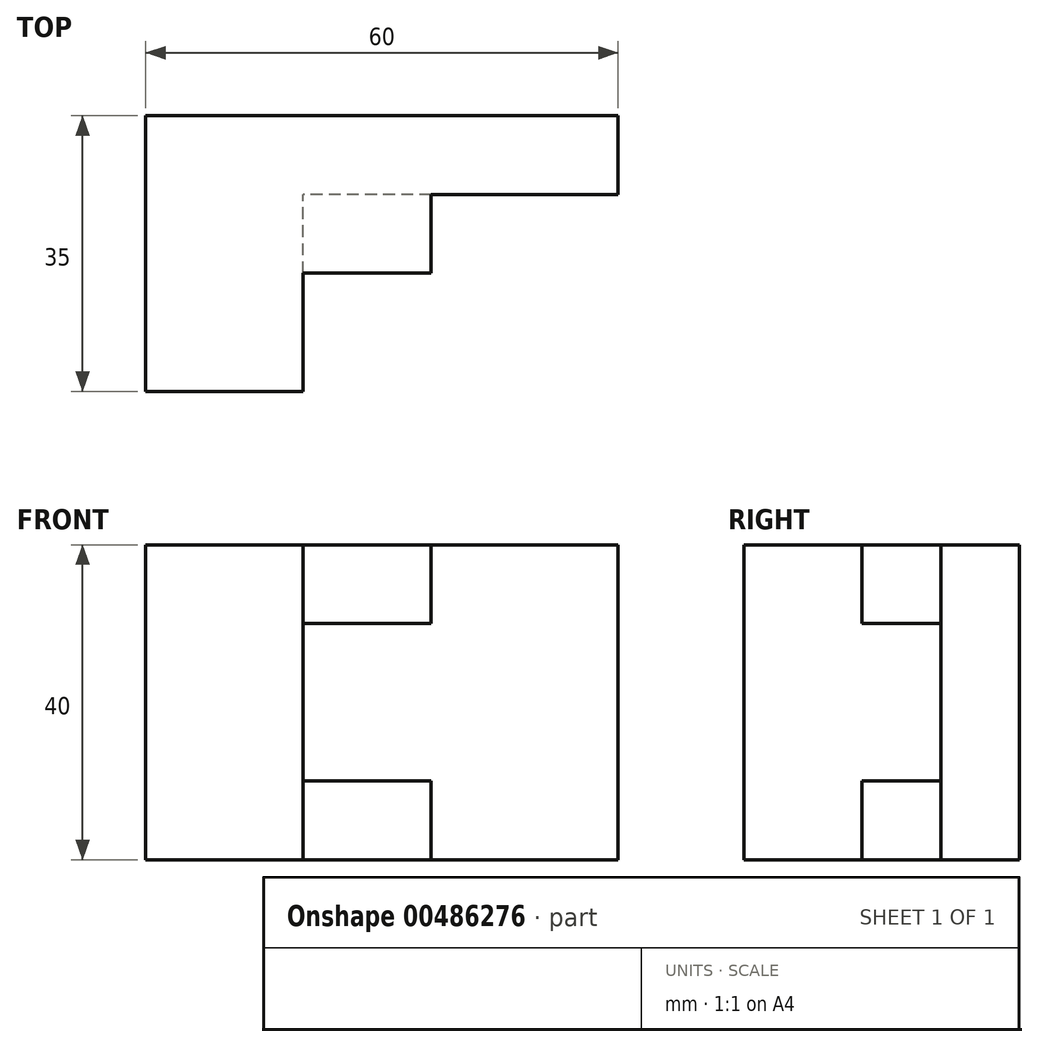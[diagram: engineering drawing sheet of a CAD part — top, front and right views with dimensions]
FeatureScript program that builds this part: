
annotation { "Feature Type Name" : "Feature", "Feature Type Description" : "" }
export const myFeature = defineFeature(function(context is Context, id is Id, definition is map)
    precondition{}
    {
        {
            var Q0;
            Q0=qCreatedBy(makeId("Front.planeOp"),FACE);
            var sketch = newSketch(context, id + "F0", { "sketchPlane" : qUnion([Q0])});
            skLineSegment(sketch, "E0", {"start": v(-36.27, 25.15) * mm, "end": v(-36.27, -14.85) * mm});
            skLineSegment(sketch, "E1", {"start": v(-36.27, -14.85) * mm, "end": v(23.73, -14.85) * mm});
            skLineSegment(sketch, "E2", {"start": v(23.73, -14.85) * mm, "end": v(23.73, 25.15) * mm});
            skLineSegment(sketch, "E3", {"start": v(23.73, 25.15) * mm, "end": v(-36.27, 25.15) * mm});
            skLineSegment(sketch, "E4", {"start": v(-36.27, -14.85) * mm, "end": v(-16.27, -14.85) * mm});
            skLineSegment(sketch, "E5", {"start": v(-16.27, -14.85) * mm, "end": v(-16.27, 25.15) * mm});
            skLineSegment(sketch, "E6", {"start": v(-16.27, 25.15) * mm, "end": v(3.73, 25.15) * mm});
            skLineSegment(sketch, "E7", {"start": v(3.73, 25.15) * mm, "end": v(3.73, 15.15) * mm});
            skLineSegment(sketch, "E8", {"start": v(3.73, 15.15) * mm, "end": v(-16.27, 15.15) * mm});
            skLineSegment(sketch, "E9", {"start": v(-16.27, -14.85) * mm, "end": v(3.73, -14.85) * mm});
            skLineSegment(sketch, "E10", {"start": v(3.73, -14.85) * mm, "end": v(3.73, -4.85) * mm});
            skLineSegment(sketch, "E11", {"start": v(3.73, -4.85) * mm, "end": v(-16.27, -4.85) * mm});
            skSolve(sketch);
        }
        {
            var Q0;
            {var subQ4=sQuery(id+"F0.wireOp",EDGE,"E0");Q0=makeQuery(id+"F0.imprint","IMPRINT",FACE,{"disambiguationData":[TD([[makeQuery(id+"F0.imprint","IMPRINT",EDGE,{"derivedFrom":subQ4}),1.0]])]});}
            var Q1;
            {var subQ3=sQuery(id+"F0.wireOp",EDGE,"E7");Q1=makeQuery(id+"F0.imprint","IMPRINT",FACE,{"disambiguationData":[TD([[makeQuery(id+"F0.imprint","IMPRINT",EDGE,{"derivedFrom":subQ3}),-1.0]])]});}
            var Q2;
            {var subQ1=sQuery(id+"F0.wireOp",EDGE,"E2");Q2=makeQuery(id+"F0.imprint","IMPRINT",FACE,{"disambiguationData":[TD([[makeQuery(id+"F0.imprint","IMPRINT",EDGE,{"derivedFrom":subQ1}),1.0]])]});}
            var Q3;
            {var subQ3=sQuery(id+"F0.wireOp",EDGE,"E10");Q3=makeQuery(id+"F0.imprint","IMPRINT",FACE,{"disambiguationData":[TD([[makeQuery(id+"F0.imprint","IMPRINT",EDGE,{"derivedFrom":subQ3}),1.0]])]});}
            extrude(context, id + "F1", {"entities" : qUnion([Q0, Q1, Q2, Q3]), "depth" : 10 * mm});
        }
        {
            var Q0;
            Q0=makeQuery(id+"F1.opExtrude","CAP_FACE",FACE,{"disambiguationData":[OSD([sQuery(id+"F0.wireOp",EDGE,"E0"),sQuery(id+"F0.wireOp",EDGE,"E1"),sQuery(id+"F0.wireOp",EDGE,"E2"),sQuery(id+"F0.wireOp",EDGE,"E3")])],"isStart":false});
            var sketch = newSketch(context, id + "F2", { "sketchPlane" : qUnion([Q0])});
            skLineSegment(sketch, "E12", {"start": v(-36.27, -14.85) * mm, "end": v(-36.27, 25.15) * mm});
            skLineSegment(sketch, "E13", {"start": v(-36.27, 25.15) * mm, "end": v(-16.27, 25.15) * mm});
            skLineSegment(sketch, "E14", {"start": v(-16.27, 25.15) * mm, "end": v(-16.27, -14.85) * mm});
            skLineSegment(sketch, "E15", {"start": v(-16.27, -14.85) * mm, "end": v(-36.27, -14.85) * mm});
            skSolve(sketch);
        }
        {
            var Q0;
            Q0=makeQuery(id+"F2.imprint","IMPRINT",FACE,{"disambiguationData":[TD([[makeQuery(id+"F2.imprint","IMPRINT",EDGE,{"derivedFrom":sQuery(id+"F2.wireOp",EDGE,"E12")}),1.0]])]});
            extrude(context, id + "F3", {"entities" : qUnion([Q0]), "operationType" : NewBodyOperationType.ADD, "depth" : 25 * mm});
        }
        {
            var Q0;
            Q0=makeQuery(id+"F1.opExtrude","CAP_FACE",FACE,{"disambiguationData":[OSD([sQuery(id+"F0.wireOp",EDGE,"E0"),sQuery(id+"F0.wireOp",EDGE,"E1"),sQuery(id+"F0.wireOp",EDGE,"E2"),sQuery(id+"F0.wireOp",EDGE,"E3")])],"isStart":false});
            var sketch = newSketch(context, id + "F4", { "sketchPlane" : qUnion([Q0])});
            skLineSegment(sketch, "E16", {"start": v(-16.27, 25.15) * mm, "end": v(0, 25.15) * mm});
            skLineSegment(sketch, "E17", {"start": v(0, 25.15) * mm, "end": v(0, 15.15) * mm});
            skLineSegment(sketch, "E18", {"start": v(0, 15.15) * mm, "end": v(-16.27, 15.15) * mm});
            skLineSegment(sketch, "E19", {"start": v(-16.27, 15.15) * mm, "end": v(-16.27, 25.15) * mm});
            skLineSegment(sketch, "E20", {"start": v(-16.27, -14.85) * mm, "end": v(0, -14.85) * mm});
            skLineSegment(sketch, "E21", {"start": v(0, -14.85) * mm, "end": v(0, -4.85) * mm});
            skLineSegment(sketch, "E22", {"start": v(0, -4.85) * mm, "end": v(-16.27, -4.85) * mm});
            skLineSegment(sketch, "E23", {"start": v(-16.27, -4.85) * mm, "end": v(-16.27, -14.85) * mm});
            skSolve(sketch);
        }
        {
            var Q0;
            Q0=makeQuery(id+"F4.imprint","IMPRINT",FACE,{"disambiguationData":[TD([[makeQuery(id+"F4.imprint","IMPRINT",EDGE,{"derivedFrom":sQuery(id+"F4.wireOp",EDGE,"E16")}),1.0]])]});
            var Q1;
            Q1=makeQuery(id+"F4.imprint","IMPRINT",FACE,{"disambiguationData":[TD([[makeQuery(id+"F4.imprint","IMPRINT",EDGE,{"derivedFrom":sQuery(id+"F4.wireOp",EDGE,"E20")}),1.0]])]});
            extrude(context, id + "F5", {"entities" : qUnion([Q0, Q1]), "operationType" : NewBodyOperationType.ADD, "depth" : 10 * mm});
        }
    });
